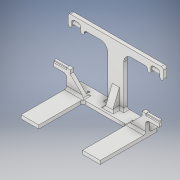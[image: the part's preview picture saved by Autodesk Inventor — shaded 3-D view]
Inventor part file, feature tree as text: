
AUTODESK INVENTOR PART (.ipt)
format: ipt  version: 2019 (Build 230136000, 136)  size: 465,408 bytes
history: native  units: in
note: dims shown in document units (in); Inventor stores cm internally (conversion verified against a paired STEP export)
features: sketch x12, extrude x10, fillet x9, reference x9, other x7, plane x2, mirror x2, projected_geometry x2, rib x1
ambient origin geometry x8: Origin, YZ Plane, XZ Plane, XY Plane, X Axis, Y Axis, Z Axis, Center Point
bodies: Solid1 (feature_tree)
feature tree (54):
  extrude  "Extrusion1"  Depth=1.0in
  extrude  "Extrusion2"  Depth=1.0in
  plane  "Work Plane2"
  extrude  "Extrusion6"  Depth=0.2in TaperAngle=0.0deg
  fillet  "Fillet3"  Radius=0.025in
  fillet  "Fillet4"  [1 undecoded]
  mirror  "Mirror1"
  rib  "Rib1"
  extrude  "Extrusion8"  Depth=0.2in
  plane  "Work Plane4"
  extrude  "Extrusion10"  Depth=0.2in TaperAngle=0.0deg
  extrude  "Extrusion11"  Depth=0.2in
  extrude  "Extrusion12"  Depth=0.125in
  extrude  "Extrusion14"  Depth=0.25in
  extrude  "Extrusion15"  Depth=0.2in
  fillet  "Fillet7"  Radius=0.01in
  mirror  "Mirror2"
  fillet  "Fillet8"  Radius=0.75in
  sketch  "Sketch5"  dims[d6=0.2in d7=0.0in d9=0.5in d10=0.0in d14=0.025in d19=90.0deg]
  fillet  "Fillet1"  Radius=0.2in
  fillet  "Fillet2"  Radius=0.2in
  fillet  "Fillet5"  Radius=0.175in
  fillet  "Fillet6"  Radius=0.2in
  fillet  "Fillet9"  Radius=0.01in
  extrude  "Extrusion16"  Depth=0.175in TaperAngle=0.0deg
  sketch  "Sketch1"  dims[d0=4.475in d2=1.0in]
  reference  "Reference1"
  sketch  "Sketch3"  dims[d4=1.0in d5=1.0in]
  other  "Work Axis1"
  sketch  "Sketch9"  dims[d22=0.45in d23=0.2in]
  projected_geometry  "Projected Loop1"
  sketch  "Sketch11"  dims[d25=0.2in d26=0.2in d27=0.0in]
  reference  "Reference4"
  reference  "Reference5"
  sketch  "Sketch12"  dims[d31=1.0in]
  reference  "Reference6"
  reference  "Reference7"
  reference  "Reference8"
  reference  "Reference9"
  sketch  "Sketch15"  dims[d32=0.1in d33=0.4in d34=0.0in d35=0.0in d36=0.1in d37=0.1in d38=0.2in]
  sketch  "Sketch17"  dims[d39=0.4in d40=0.125in]
  projected_geometry  "Projected Loop2"
  sketch  "Sketch18"  dims[d41=75.0deg d42=0.25in]
  sketch  "Sketch20"  dims[d43=0.4in d44=0.175in d45=0.01in d46=0.75in d47=0.0in d51=0.2in d53=0.2in d54=0.0in d57=0.175in d58=0.0in d60=0.2in d61=0.01in]
  sketch  "Sketch21"  dims[d62=0.1in d63=0.175in d64=0.0in]
  sketch  "Sketch22"  dims[d67=1.0in d68=0.0in d69=0.8in d70=1.0in d71=0.0in d72=0.125in d73=0.3in d74=1.0in d75=0.0in]
  reference  "Reference10"
  reference  "Reference11"
  other  "<userpath>\OneDrive\Documents\Inventor\Mr.Green\Mr.Green.iam"
  other  "Mr.Green.iam"
  other  "Chassis:1"
  other  "Shock_Arm:1"
  other  "Shock_Absorber:1"
  other  "Top:1"
note: 1 required parameter value undecoded (feature->parameter linkage not recoverable at this tier; creation-order binding heuristic only, values carry confidence <= 0.55)
